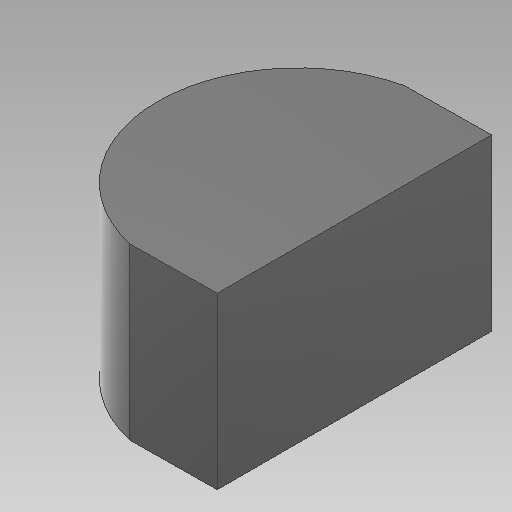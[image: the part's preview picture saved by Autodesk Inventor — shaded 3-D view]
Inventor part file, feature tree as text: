
AUTODESK INVENTOR PART (.ipt)
format: ipt  version: 2020 (Build 240168000, 168)  size: 153,088 bytes
history: native  units: in
note: dims shown in document units (in); Inventor stores cm internally (conversion verified against a paired STEP export)
features: extrude x6, sketch x5
ambient origin geometry x8: Origin, YZ Plane, XZ Plane, XY Plane, X Axis, Y Axis, Z Axis, Center Point
bodies: Solid1 (feature_tree)
feature tree (11):
  extrude  "Extrusion1"  Depth=1.9685in
  extrude  "Extrusion2"  Depth=2.4409in
  extrude  "Extrusion3"  TaperAngle=90.0deg  [1 undecoded]
  sketch  "Sketch4"  dims[d7=2.4409in d8=0.0in d9=0.7874in]
  extrude  "Extrusion4"  Depth=2.4409in
  extrude  "Extrusion5"  TaperAngle=120.0deg  [1 undecoded]
  extrude  "Extrusion6"  Depth=2.4409in
  sketch  "Sketch1"  dims[d0=1.9685in d1=7.874in]
  sketch  "Sketch2"  dims[d2=2.4409in d3=0.0in d4=1.5748in]
  sketch  "Sketch3"  dims[d5=0.7874in d6=90.0deg]
  sketch  "Sketch5"  dims[d10=2.3622in d11=120.0deg d12=0.7874in d13=2.3622in d14=120.0deg d15=2.4409in d16=0.0in d17=2.4409in d18=0.0in d19=2.4409in d20=0.0in d21=90.0deg d22=2.4409in d23=0.0in]
note: 2 required parameter values undecoded (feature->parameter linkage not recoverable at this tier; creation-order binding heuristic only, values carry confidence <= 0.55)
